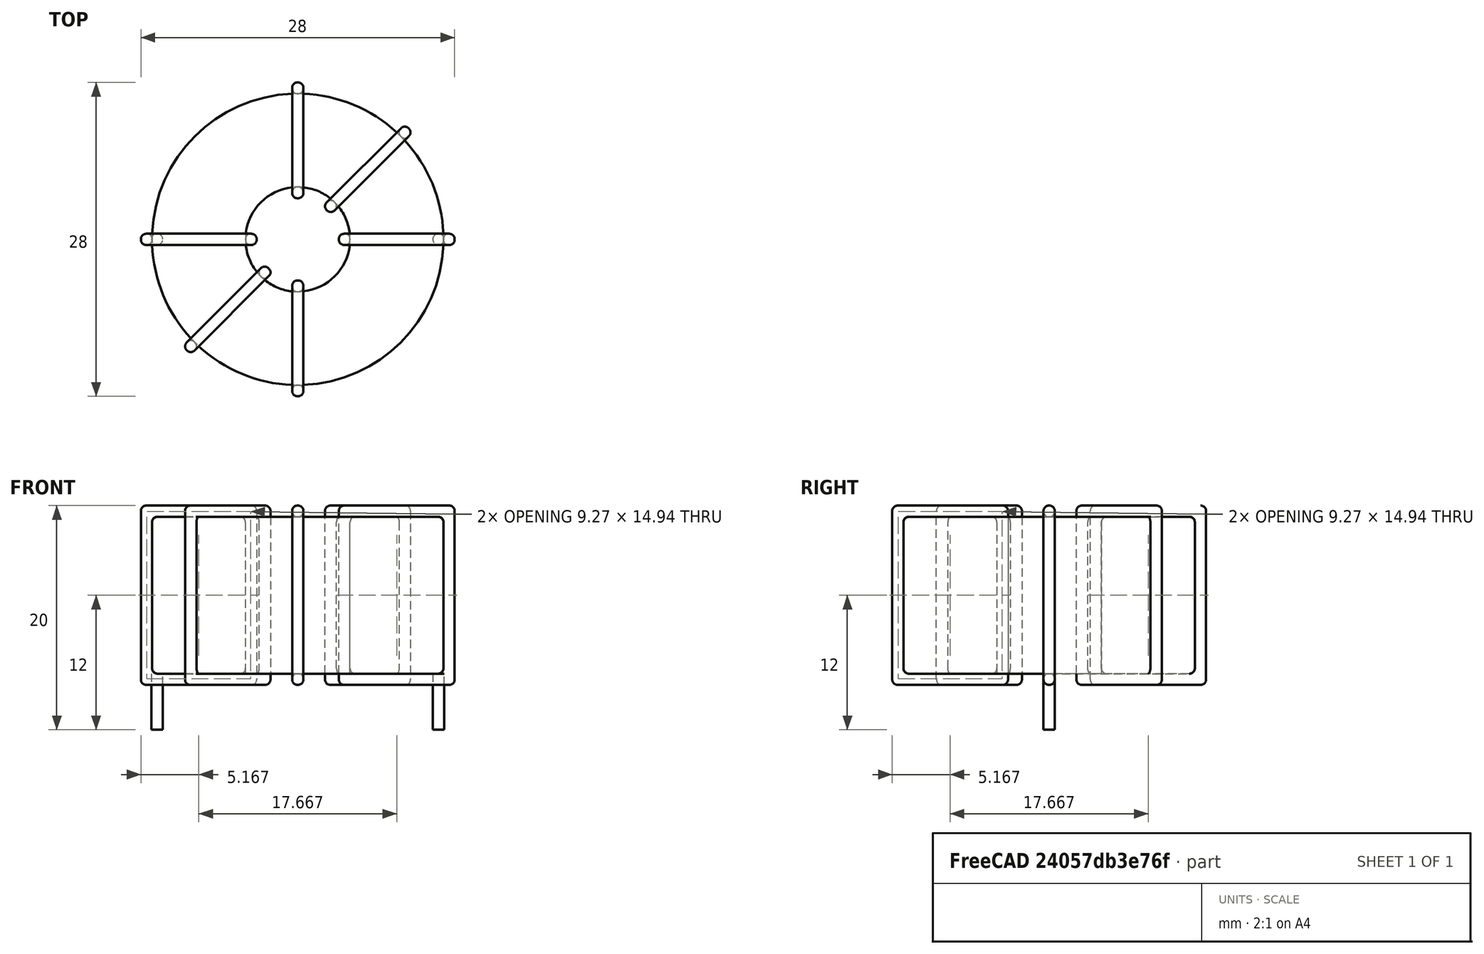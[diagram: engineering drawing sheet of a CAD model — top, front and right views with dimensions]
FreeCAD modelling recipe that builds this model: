
FCSTD DOCUMENT  (FreeCAD 0.16R6703 (Git))
Label: L_Toroid_Horizontal_D28.0mm_P25.10mm_Bourns_2200series
License: All rights reserved
LicenseURL: http://en.wikipedia.org/wiki/All_rights_reserved
objects: Sketcher::SketchObject×6, PartDesign::Pad×6, PartDesign::Fillet×5, Spreadsheet::Sheet×1
note: 23 computed .brp shape members not serialized (recipe doc carries the construction recipe); baked Part::Feature solids carry a one-line shape summary decoded from their .brp

FEATURE [Spreadsheet::Sheet] Spreadsheet  label="dimensions"
  cells = A1=Wx; B1(Wx)=28; C1(WW)=9.333333333333334; D1=28; A2=Wy; B2(Wy)=28; D2=28; A3=RM; B3(RMx)=25.1; C3(RMy)=0; A4=d_wire; B4(d_wire)=1; A5=H; B5(H)=14; A6=offsetx; B6(offsetx)=1.449999999999999
FEATURE [Sketcher::SketchObject] Sketch
  Placement = pos=(0,0,1.5) rot=(0,0,1;0rad)
  expr: Placement.Base.z = 0.5 + Spreadsheet.d_wire
  expr: Constraints[0] = Spreadsheet.Wx / 2 - Spreadsheet.d_wire
  expr: Constraints[4] = Spreadsheet.WW / 2
  expr: Constraints[2] = Spreadsheet.RMy / 2
  expr: Constraints[1] = Spreadsheet.RMx / 2
  sketch-geometry (2):
    g0: Circle CenterX=12.55 CenterY=0 CenterZ=0 NormalX=0 NormalY=0 NormalZ=1 Radius=13
    g1: Circle CenterX=12.55 CenterY=0 CenterZ=0 NormalX=0 NormalY=0 NormalZ=1 Radius=4.66667
  constraints (5):
    c: Radius(g0) = 13
    c: DistanceX(g-1,g0) = 12.55
    c: DistanceY(g-1,g0) = 0
    c: Coincident(g1,g0)
    c: Radius(g1) = 4.66667
FEATURE [PartDesign::Pad] Pad
  Length = 14
  Length2 = 100
  Placement = pos=(0,0,1.5) rot=(0,0,1;0rad)
  Sketch = -> Sketch
  Type = 0
  expr: Length = Spreadsheet.H
FEATURE [Sketcher::SketchObject] Sketch001
  Placement = pos=(0,0,1) rot=(0,0,1;0rad)
  expr: Placement.Base.z = 0.5 + Spreadsheet.d_wire * 0.5
  expr: Constraints[4] = Spreadsheet.RMx
  expr: Constraints[2] = Spreadsheet.RMy
  expr: Constraints[1] = Spreadsheet.d_wire / 2
  sketch-geometry (2):
    g0: Circle CenterX=0 CenterY=0 CenterZ=0 NormalX=0 NormalY=0 NormalZ=1 Radius=0.5
    g1: Circle CenterX=25.1 CenterY=0 CenterZ=0 NormalX=0 NormalY=0 NormalZ=1 Radius=0.5
  constraints (5):
    c: Equal(g0,g1)
    c: Radius(g0) = 0.5
    c: DistanceY(g-1,g1) = 0
    c: Coincident(g0,g-1)
    c: DistanceX(g-1,g1) = 25.1
FEATURE [PartDesign::Pad] Pad001
  Length = 0.5
  Length2 = 4.5
  Placement = pos=(0,0,1) rot=(0,0,1;0rad)
  Reversed = true
  Sketch = -> Sketch001
  Type = 4
  expr: Length2 = 3.5 + Spreadsheet.d_wire
  expr: Length = Spreadsheet.d_wire / 2
FEATURE [PartDesign::Fillet] Fillet
  Base = -> Pad [Edge6,Edge3,Edge2]
  Placement = pos=(0,0,1.5) rot=(0,0,1;0rad)
  Radius = 0.5
FEATURE [Sketcher::SketchObject] Sketch003
  Placement = pos=(12.55,0,0) rot=(1,0,0;1.5708rad)
  expr: Placement.Base.x = Spreadsheet.RMx / 2
  expr: Constraints[49] = Spreadsheet.Wx - Spreadsheet.d_wire * 2
  expr: Constraints[44] = Spreadsheet.d_wire
  expr: Constraints[23] = Spreadsheet.H
  expr: Constraints[22] = Spreadsheet.Wx / 2 - Spreadsheet.d_wire
  expr: Placement.Base.y = Spreadsheet.RMy / 2
  expr: Constraints[21] = (Spreadsheet.Wx - Spreadsheet.WW) / 2 - Spreadsheet.d_wire
  expr: Constraints[19] = Spreadsheet.d_wire
  expr: Constraints[17] = Spreadsheet.d_wire
  expr: Constraints[18] = Spreadsheet.d_wire
  expr: Constraints[16] = Spreadsheet.d_wire
  sketch-geometry (16):
    g0: LineSegment StartX=-3.66667 StartY=0.5 StartZ=0 EndX=-14 EndY=0.5 EndZ=0
    g1: LineSegment StartX=-14 StartY=0.5 StartZ=0 EndX=-14 EndY=16.5 EndZ=0
    g2: LineSegment StartX=-14 StartY=16.5 StartZ=0 EndX=-3.66667 EndY=16.5 EndZ=0
    g3: LineSegment StartX=-3.66667 StartY=16.5 StartZ=0 EndX=-3.66667 EndY=0.5 EndZ=0
    g4: LineSegment StartX=-13 StartY=15.5 StartZ=0 EndX=-4.66667 EndY=15.5 EndZ=0
    g5: LineSegment StartX=-4.66667 StartY=15.5 StartZ=0 EndX=-4.66667 EndY=1.5 EndZ=0
    g6: LineSegment StartX=-4.66667 StartY=1.5 StartZ=0 EndX=-13 EndY=1.5 EndZ=0
    g7: LineSegment StartX=-13 StartY=1.5 StartZ=0 EndX=-13 EndY=15.5 EndZ=0
    g8: LineSegment StartX=3.66667 StartY=16.5 StartZ=0 EndX=14 EndY=16.5 EndZ=0
    g9: LineSegment StartX=14 StartY=16.5 StartZ=0 EndX=14 EndY=0.5 EndZ=0
    g10: LineSegment StartX=14 StartY=0.5 StartZ=0 EndX=3.66667 EndY=0.5 EndZ=0
    g11: LineSegment StartX=3.66667 StartY=0.5 StartZ=0 EndX=3.66667 EndY=16.5 EndZ=0
    g12: LineSegment StartX=4.66667 StartY=15.5 StartZ=0 EndX=13 EndY=15.5 EndZ=0
    g13: LineSegment StartX=13 StartY=15.5 StartZ=0 EndX=13 EndY=1.5 EndZ=0
    g14: LineSegment StartX=13 StartY=1.5 StartZ=0 EndX=4.66667 EndY=1.5 EndZ=0
    g15: LineSegment StartX=4.66667 StartY=1.5 StartZ=0 EndX=4.66667 EndY=15.5 EndZ=0
  constraints (50):
    c: Horizontal(g0)
    c: Coincident(g1,g0)
    c: Vertical(g1)
    c: Coincident(g2,g1)
    c: Horizontal(g2)
    c: Coincident(g3,g2)
    c: Coincident(g3,g0)
    c: Vertical(g3)
    c: Coincident(g4,g5)
    c: Coincident(g5,g6)
    c: Coincident(g6,g7)
    c: Coincident(g7,g4)
    c: Horizontal(g4)
    c: Horizontal(g6)
    c: Vertical(g5)
    c: Vertical(g7)
    c: DistanceX(g1,g4) = 1
    c: DistanceY(g4,g1) = 1
    c: DistanceX(g5,g0) = 1
    c: DistanceY(g0,g5) = 1
    c: DistanceY(g-1,g0) = 0.5
    c: DistanceX(g6,g6) = 8.33333
    c: DistanceX(g6,g-1) = 13
    c: DistanceY(g7,g7) = 14
    c: Coincident(g8,g9)
    c: Coincident(g9,g10)
    c: Coincident(g10,g11)
    c: Coincident(g11,g8)
    c: Horizontal(g8)
    c: Horizontal(g10)
    c: Vertical(g9)
    c: Vertical(g11)
    c: Coincident(g12,g13)
    c: Coincident(g13,g14)
    c: Coincident(g14,g15)
    c: Coincident(g15,g12)
    c: Horizontal(g12)
    c: Horizontal(g14)
    c: Vertical(g13)
    c: Vertical(g15)
    c: DistanceY(g8,g2) = 0
    c: DistanceY(g10,g0) = 0
    c: DistanceY(g14,g5) = 0
    c: DistanceY(g12,g4) = 0
    c: DistanceX(g8,g12) = 1
    c: Equal(g8,g2)
    c: Equal(g12,g4)
    c: Equal(g9,g1)
    c: Equal(g13,g7)
    c: DistanceX(g4,g12) = 26
FEATURE [PartDesign::Pad] Pad002
  Length = 1
  Length2 = 100
  Midplane = true
  Placement = pos=(12.55,0,0) rot=(1,0,0;1.5708rad)
  Sketch = -> Sketch003
  Type = 0
  expr: Length = Spreadsheet.d_wire
FEATURE [PartDesign::Fillet] Fillet001
  Base = -> Pad002 [Edge38,Edge41,Edge42,Edge43,Edge29,Edge32,Edge33,Edge34,Edge25,Edge35,Edge36,Edge13,Edge14,Edge15,Edge16,Edge17,Edge18,Edge19,Edge1,Edge2,Edge3,Edge4,Edge5,Edge6,Edge7,Edge37,Edge39,Edge40,Edge20,Edge23,Edge24,Edge21,Edge22,Edge8,Edge9,Edge10,Edge11,Edge12,Edge26,Edge27,+8 more]
  Placement = pos=(12.55,0,0) rot=(1,0,0;1.5708rad)
  Radius = 0.47
  expr: Radius = Spreadsheet.d_wire * 0.47
FEATURE [Sketcher::SketchObject] Sketch004
  Placement = pos=(12.55,0,0) rot=(0.862856,0.357407,0.357407;1.71777rad)
  expr: Placement.Base.x = Spreadsheet.RMx / 2
  expr: Constraints[49] = Spreadsheet.Wx - 2 * Spreadsheet.d_wire
  expr: Constraints[44] = Spreadsheet.d_wire
  expr: Constraints[23] = Spreadsheet.H
  expr: Constraints[22] = Spreadsheet.Wx / 2 - Spreadsheet.d_wire
  expr: Placement.Base.y = Spreadsheet.RMy / 2
  expr: Constraints[21] = (Spreadsheet.Wx - Spreadsheet.WW) / 2 - Spreadsheet.d_wire
  expr: Constraints[19] = Spreadsheet.d_wire
  expr: Constraints[17] = Spreadsheet.d_wire
  expr: Constraints[18] = Spreadsheet.d_wire
  expr: Constraints[16] = Spreadsheet.d_wire
  sketch-geometry (16):
    g0: LineSegment StartX=-3.66667 StartY=0.5 StartZ=0 EndX=-14 EndY=0.5 EndZ=0
    g1: LineSegment StartX=-14 StartY=0.5 StartZ=0 EndX=-14 EndY=16.5 EndZ=0
    g2: LineSegment StartX=-14 StartY=16.5 StartZ=0 EndX=-3.66667 EndY=16.5 EndZ=0
    g3: LineSegment StartX=-3.66667 StartY=16.5 StartZ=0 EndX=-3.66667 EndY=0.5 EndZ=0
    g4: LineSegment StartX=-13 StartY=15.5 StartZ=0 EndX=-4.66667 EndY=15.5 EndZ=0
    g5: LineSegment StartX=-4.66667 StartY=15.5 StartZ=0 EndX=-4.66667 EndY=1.5 EndZ=0
    g6: LineSegment StartX=-4.66667 StartY=1.5 StartZ=0 EndX=-13 EndY=1.5 EndZ=0
    g7: LineSegment StartX=-13 StartY=1.5 StartZ=0 EndX=-13 EndY=15.5 EndZ=0
    g8: LineSegment StartX=3.66667 StartY=16.5 StartZ=0 EndX=14 EndY=16.5 EndZ=0
    g9: LineSegment StartX=14 StartY=16.5 StartZ=0 EndX=14 EndY=0.5 EndZ=0
    g10: LineSegment StartX=14 StartY=0.5 StartZ=0 EndX=3.66667 EndY=0.5 EndZ=0
    g11: LineSegment StartX=3.66667 StartY=0.5 StartZ=0 EndX=3.66667 EndY=16.5 EndZ=0
    g12: LineSegment StartX=4.66667 StartY=15.5 StartZ=0 EndX=13 EndY=15.5 EndZ=0
    g13: LineSegment StartX=13 StartY=15.5 StartZ=0 EndX=13 EndY=1.5 EndZ=0
    g14: LineSegment StartX=13 StartY=1.5 StartZ=0 EndX=4.66667 EndY=1.5 EndZ=0
    g15: LineSegment StartX=4.66667 StartY=1.5 StartZ=0 EndX=4.66667 EndY=15.5 EndZ=0
  constraints (50):
    c: Horizontal(g0)
    c: Coincident(g1,g0)
    c: Vertical(g1)
    c: Coincident(g2,g1)
    c: Horizontal(g2)
    c: Coincident(g3,g2)
    c: Coincident(g3,g0)
    c: Vertical(g3)
    c: Coincident(g4,g5)
    c: Coincident(g5,g6)
    c: Coincident(g6,g7)
    c: Coincident(g7,g4)
    c: Horizontal(g4)
    c: Horizontal(g6)
    c: Vertical(g5)
    c: Vertical(g7)
    c: DistanceX(g1,g4) = 1
    c: DistanceY(g4,g1) = 1
    c: DistanceX(g5,g0) = 1
    c: DistanceY(g0,g5) = 1
    c: DistanceY(g-1,g0) = 0.5
    c: DistanceX(g6,g6) = 8.33333
    c: DistanceX(g6,g-1) = 13
    c: DistanceY(g7,g7) = 14
    c: Coincident(g8,g9)
    c: Coincident(g9,g10)
    c: Coincident(g10,g11)
    c: Coincident(g11,g8)
    c: Horizontal(g8)
    c: Horizontal(g10)
    c: Vertical(g9)
    c: Vertical(g11)
    c: Coincident(g12,g13)
    c: Coincident(g13,g14)
    c: Coincident(g14,g15)
    c: Coincident(g15,g12)
    c: Horizontal(g12)
    c: Horizontal(g14)
    c: Vertical(g13)
    c: Vertical(g15)
    c: DistanceY(g8,g2) = 0
    c: DistanceY(g10,g0) = 0
    c: DistanceY(g14,g5) = 0
    c: DistanceY(g12,g4) = 0
    c: DistanceX(g8,g12) = 1
    c: Equal(g8,g2)
    c: Equal(g12,g4)
    c: Equal(g9,g1)
    c: Equal(g13,g7)
    c: DistanceX(g4,g12) = 26
FEATURE [PartDesign::Pad] Pad003
  Length = 1
  Length2 = 100
  Midplane = true
  Placement = pos=(12.55,0,0) rot=(0.862856,0.357407,0.357407;1.71777rad)
  Sketch = -> Sketch004
  Type = 0
  expr: Length = Spreadsheet.d_wire
FEATURE [PartDesign::Fillet] Fillet002
  Base = -> Pad003 [Edge38,Edge41,Edge42,Edge43,Edge29,Edge32,Edge33,Edge34,Edge25,Edge35,Edge36,Edge13,Edge14,Edge15,Edge16,Edge17,Edge18,Edge19,Edge1,Edge2,Edge3,Edge4,Edge5,Edge6,Edge7,Edge37,Edge39,Edge40,Edge20,Edge23,Edge24,Edge21,Edge22,Edge8,Edge9,Edge10,Edge11,Edge12,Edge26,Edge27,+8 more]
  Placement = pos=(12.55,0,0) rot=(0.862856,0.357407,0.357407;1.71777rad)
  Radius = 0.47
  expr: Radius = Spreadsheet.d_wire * 0.47
FEATURE [Sketcher::SketchObject] Sketch005
  Placement = pos=(12.55,0,0) rot=(0.862856,-0.357407,-0.357407;1.71777rad)
  expr: Placement.Base.x = Spreadsheet.RMx / 2
  expr: Constraints[49] = Spreadsheet.Wx - 2 * Spreadsheet.d_wire
  expr: Constraints[44] = Spreadsheet.d_wire
  expr: Constraints[23] = Spreadsheet.H
  expr: Constraints[22] = Spreadsheet.Wx / 2 - Spreadsheet.d_wire
  expr: Placement.Base.y = Spreadsheet.RMy / 2
  expr: Constraints[21] = (Spreadsheet.Wx - Spreadsheet.WW) / 2 - Spreadsheet.d_wire
  expr: Constraints[19] = Spreadsheet.d_wire
  expr: Constraints[17] = Spreadsheet.d_wire
  expr: Constraints[18] = Spreadsheet.d_wire
  expr: Constraints[16] = Spreadsheet.d_wire
  sketch-geometry (16):
    g0: LineSegment StartX=-3.66667 StartY=0.5 StartZ=0 EndX=-14 EndY=0.5 EndZ=0
    g1: LineSegment StartX=-14 StartY=0.5 StartZ=0 EndX=-14 EndY=16.5 EndZ=0
    g2: LineSegment StartX=-14 StartY=16.5 StartZ=0 EndX=-3.66667 EndY=16.5 EndZ=0
    g3: LineSegment StartX=-3.66667 StartY=16.5 StartZ=0 EndX=-3.66667 EndY=0.5 EndZ=0
    g4: LineSegment StartX=-13 StartY=15.5 StartZ=0 EndX=-4.66667 EndY=15.5 EndZ=0
    g5: LineSegment StartX=-4.66667 StartY=15.5 StartZ=0 EndX=-4.66667 EndY=1.5 EndZ=0
    g6: LineSegment StartX=-4.66667 StartY=1.5 StartZ=0 EndX=-13 EndY=1.5 EndZ=0
    g7: LineSegment StartX=-13 StartY=1.5 StartZ=0 EndX=-13 EndY=15.5 EndZ=0
    g8: LineSegment StartX=3.66667 StartY=16.5 StartZ=0 EndX=14 EndY=16.5 EndZ=0
    g9: LineSegment StartX=14 StartY=16.5 StartZ=0 EndX=14 EndY=0.5 EndZ=0
    g10: LineSegment StartX=14 StartY=0.5 StartZ=0 EndX=3.66667 EndY=0.5 EndZ=0
    g11: LineSegment StartX=3.66667 StartY=0.5 StartZ=0 EndX=3.66667 EndY=16.5 EndZ=0
    g12: LineSegment StartX=4.66667 StartY=15.5 StartZ=0 EndX=13 EndY=15.5 EndZ=0
    g13: LineSegment StartX=13 StartY=15.5 StartZ=0 EndX=13 EndY=1.5 EndZ=0
    g14: LineSegment StartX=13 StartY=1.5 StartZ=0 EndX=4.66667 EndY=1.5 EndZ=0
    g15: LineSegment StartX=4.66667 StartY=1.5 StartZ=0 EndX=4.66667 EndY=15.5 EndZ=0
  constraints (50):
    c: Horizontal(g0)
    c: Coincident(g1,g0)
    c: Vertical(g1)
    c: Coincident(g2,g1)
    c: Horizontal(g2)
    c: Coincident(g3,g2)
    c: Coincident(g3,g0)
    c: Vertical(g3)
    c: Coincident(g4,g5)
    c: Coincident(g5,g6)
    c: Coincident(g6,g7)
    c: Coincident(g7,g4)
    c: Horizontal(g4)
    c: Horizontal(g6)
    c: Vertical(g5)
    c: Vertical(g7)
    c: DistanceX(g1,g4) = 1
    c: DistanceY(g4,g1) = 1
    c: DistanceX(g5,g0) = 1
    c: DistanceY(g0,g5) = 1
    c: DistanceY(g-1,g0) = 0.5
    c: DistanceX(g6,g6) = 8.33333
    c: DistanceX(g6,g-1) = 13
    c: DistanceY(g7,g7) = 14
    c: Coincident(g8,g9)
    c: Coincident(g9,g10)
    c: Coincident(g10,g11)
    c: Coincident(g11,g8)
    c: Horizontal(g8)
    c: Horizontal(g10)
    c: Vertical(g9)
    c: Vertical(g11)
    c: Coincident(g12,g13)
    c: Coincident(g13,g14)
    c: Coincident(g14,g15)
    c: Coincident(g15,g12)
    c: Horizontal(g12)
    c: Horizontal(g14)
    c: Vertical(g13)
    c: Vertical(g15)
    c: DistanceY(g8,g2) = 0
    c: DistanceY(g10,g0) = 0
    c: DistanceY(g14,g5) = 0
    c: DistanceY(g12,g4) = 0
    c: DistanceX(g8,g12) = 1
    c: Equal(g8,g2)
    c: Equal(g12,g4)
    c: Equal(g9,g1)
    c: Equal(g13,g7)
    c: DistanceX(g4,g12) = 26
FEATURE [PartDesign::Pad] Pad004
  Length = 1
  Length2 = 100
  Midplane = true
  Placement = pos=(12.55,0,0) rot=(0.862856,-0.357407,-0.357407;1.71777rad)
  Sketch = -> Sketch005
  Type = 0
  expr: Length = Spreadsheet.d_wire
FEATURE [PartDesign::Fillet] Fillet003
  Base = -> Pad004 [Edge38,Edge41,Edge42,Edge43,Edge29,Edge32,Edge33,Edge34,Edge25,Edge35,Edge36,Edge13,Edge14,Edge15,Edge16,Edge17,Edge18,Edge19,Edge1,Edge2,Edge3,Edge4,Edge5,Edge6,Edge7,Edge37,Edge39,Edge40,Edge20,Edge23,Edge24,Edge21,Edge22,Edge8,Edge9,Edge10,Edge11,Edge12,Edge26,Edge27,+8 more]
  Placement = pos=(12.55,0,0) rot=(0.862856,-0.357407,-0.357407;1.71777rad)
  Radius = 0.47
  expr: Radius = Spreadsheet.d_wire * 0.47
FEATURE [Sketcher::SketchObject] Sketch006
  Placement = pos=(12.55,0,0) rot=(0.57735,0.57735,0.57735;2.0944rad)
  expr: Placement.Base.x = Spreadsheet.RMx / 2
  expr: Constraints[49] = Spreadsheet.Wx - Spreadsheet.d_wire * 2
  expr: Constraints[44] = Spreadsheet.d_wire
  expr: Constraints[23] = Spreadsheet.H
  expr: Constraints[22] = Spreadsheet.Wx / 2 - Spreadsheet.d_wire
  expr: Placement.Base.y = Spreadsheet.RMy / 2
  expr: Constraints[21] = (Spreadsheet.Wx - Spreadsheet.WW) / 2 - Spreadsheet.d_wire
  expr: Constraints[19] = Spreadsheet.d_wire
  expr: Constraints[17] = Spreadsheet.d_wire
  expr: Constraints[18] = Spreadsheet.d_wire
  expr: Constraints[16] = Spreadsheet.d_wire
  sketch-geometry (16):
    g0: LineSegment StartX=-3.66667 StartY=0.5 StartZ=0 EndX=-14 EndY=0.5 EndZ=0
    g1: LineSegment StartX=-14 StartY=0.5 StartZ=0 EndX=-14 EndY=16.5 EndZ=0
    g2: LineSegment StartX=-14 StartY=16.5 StartZ=0 EndX=-3.66667 EndY=16.5 EndZ=0
    g3: LineSegment StartX=-3.66667 StartY=16.5 StartZ=0 EndX=-3.66667 EndY=0.5 EndZ=0
    g4: LineSegment StartX=-13 StartY=15.5 StartZ=0 EndX=-4.66667 EndY=15.5 EndZ=0
    g5: LineSegment StartX=-4.66667 StartY=15.5 StartZ=0 EndX=-4.66667 EndY=1.5 EndZ=0
    g6: LineSegment StartX=-4.66667 StartY=1.5 StartZ=0 EndX=-13 EndY=1.5 EndZ=0
    g7: LineSegment StartX=-13 StartY=1.5 StartZ=0 EndX=-13 EndY=15.5 EndZ=0
    g8: LineSegment StartX=3.66667 StartY=16.5 StartZ=0 EndX=14 EndY=16.5 EndZ=0
    g9: LineSegment StartX=14 StartY=16.5 StartZ=0 EndX=14 EndY=0.5 EndZ=0
    g10: LineSegment StartX=14 StartY=0.5 StartZ=0 EndX=3.66667 EndY=0.5 EndZ=0
    g11: LineSegment StartX=3.66667 StartY=0.5 StartZ=0 EndX=3.66667 EndY=16.5 EndZ=0
    g12: LineSegment StartX=4.66667 StartY=15.5 StartZ=0 EndX=13 EndY=15.5 EndZ=0
    g13: LineSegment StartX=13 StartY=15.5 StartZ=0 EndX=13 EndY=1.5 EndZ=0
    g14: LineSegment StartX=13 StartY=1.5 StartZ=0 EndX=4.66667 EndY=1.5 EndZ=0
    g15: LineSegment StartX=4.66667 StartY=1.5 StartZ=0 EndX=4.66667 EndY=15.5 EndZ=0
  constraints (50):
    c: Horizontal(g0)
    c: Coincident(g1,g0)
    c: Vertical(g1)
    c: Coincident(g2,g1)
    c: Horizontal(g2)
    c: Coincident(g3,g2)
    c: Coincident(g3,g0)
    c: Vertical(g3)
    c: Coincident(g4,g5)
    c: Coincident(g5,g6)
    c: Coincident(g6,g7)
    c: Coincident(g7,g4)
    c: Horizontal(g4)
    c: Horizontal(g6)
    c: Vertical(g5)
    c: Vertical(g7)
    c: DistanceX(g1,g4) = 1
    c: DistanceY(g4,g1) = 1
    c: DistanceX(g5,g0) = 1
    c: DistanceY(g0,g5) = 1
    c: DistanceY(g-1,g0) = 0.5
    c: DistanceX(g6,g6) = 8.33333
    c: DistanceX(g6,g-1) = 13
    c: DistanceY(g7,g7) = 14
    c: Coincident(g8,g9)
    c: Coincident(g9,g10)
    c: Coincident(g10,g11)
    c: Coincident(g11,g8)
    c: Horizontal(g8)
    c: Horizontal(g10)
    c: Vertical(g9)
    c: Vertical(g11)
    c: Coincident(g12,g13)
    c: Coincident(g13,g14)
    c: Coincident(g14,g15)
    c: Coincident(g15,g12)
    c: Horizontal(g12)
    c: Horizontal(g14)
    c: Vertical(g13)
    c: Vertical(g15)
    c: DistanceY(g8,g2) = 0
    c: DistanceY(g10,g0) = 0
    c: DistanceY(g14,g5) = 0
    c: DistanceY(g12,g4) = 0
    c: DistanceX(g8,g12) = 1
    c: Equal(g8,g2)
    c: Equal(g12,g4)
    c: Equal(g9,g1)
    c: Equal(g13,g7)
    c: DistanceX(g4,g12) = 26
FEATURE [PartDesign::Pad] Pad005
  Length = 1
  Length2 = 100
  Midplane = true
  Placement = pos=(12.55,0,0) rot=(0.57735,0.57735,0.57735;2.0944rad)
  Sketch = -> Sketch006
  Type = 0
  expr: Length = Spreadsheet.d_wire
FEATURE [PartDesign::Fillet] Fillet004
  Base = -> Pad005 [Edge38,Edge41,Edge42,Edge43,Edge29,Edge32,Edge33,Edge34,Edge25,Edge35,Edge36,Edge13,Edge14,Edge15,Edge16,Edge17,Edge18,Edge19,Edge1,Edge2,Edge3,Edge4,Edge5,Edge6,Edge7,Edge37,Edge39,Edge40,Edge20,Edge23,Edge24,Edge21,Edge22,Edge8,Edge9,Edge10,Edge11,Edge12,Edge26,Edge27,+8 more]
  Placement = pos=(12.55,0,0) rot=(0.57735,0.57735,0.57735;2.0944rad)
  Radius = 0.47
  expr: Radius = Spreadsheet.d_wire * 0.47
